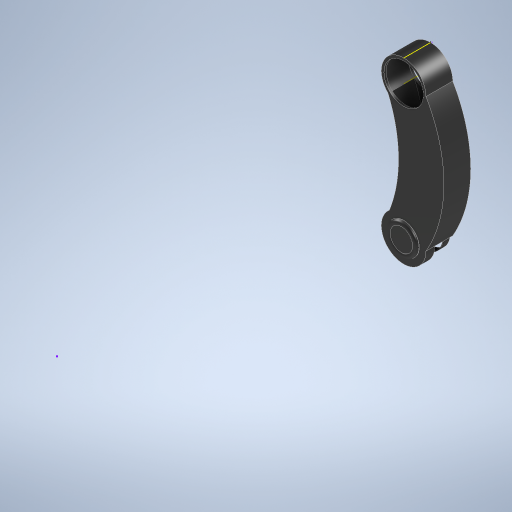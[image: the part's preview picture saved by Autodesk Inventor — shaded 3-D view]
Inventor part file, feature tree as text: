
AUTODESK INVENTOR PART (.ipt)
format: ipt  version: 2024 (Build 280153000, 153)  size: 354,816 bytes
history: native  units: mm
features: extrude x8, sketch x6, shell x1, fillet x1
ambient origin geometry x8: Origin, YZ Plane, XZ Plane, XY Plane, X Axis, Y Axis, Z Axis, Center Point
bodies: Solid1 (feature_tree)
feature tree (16):
  sketch  "Sketch1"  dims[d0=100.0mm d1=88.0mm]
  extrude  "Extrusion1"  Depth=88.0mm
  extrude  "Extrusion2"  Depth=20.0mm TaperAngle=0.0deg
  extrude  "Extrusion3"  Depth=40.0mm
  extrude  "Extrusion4"  Depth=50.0mm TaperAngle=0.0deg
  extrude  "Extrusion5"  Depth=60.0mm
  shell  "Shell1"  Thickness=60.0mm
  sketch  "Sketch5"  dims[d13=100.0mm d14=88.0mm d15=60.0mm d16=0.0mm]
  extrude  "Extrusion6"  Depth=5.0mm
  extrude  "Extrusion7"  Depth=300.0mm
  extrude  "Extrusion8"  Depth=50.0mm
  fillet  "Fillet1"  Radius=10.0mm
  sketch  "Sketch6"  dims[d17=10.0mm d18=0.0mm d19=5.0mm d20=70.0mm d21=50.0mm d22=10.0mm d23=0.0mm d24=5.0mm d25=0.0mm d26=5.0mm d27=0.0mm d28=6.0mm d29=300.0mm d30=300.0mm d31=0.5mm d32=0.872665mm d33=0.5mm d34=0.872665mm]
  sketch  "Sketch2"  dims[d2=85.0mm d3=20.0mm d4=0.0mm]
  sketch  "Sketch3"  dims[d5=40.0mm d6=0.0mm d7=100.0mm]
  sketch  "Sketch4"  dims[d8=25.0mm d9=50.0mm d10=0.0mm]
